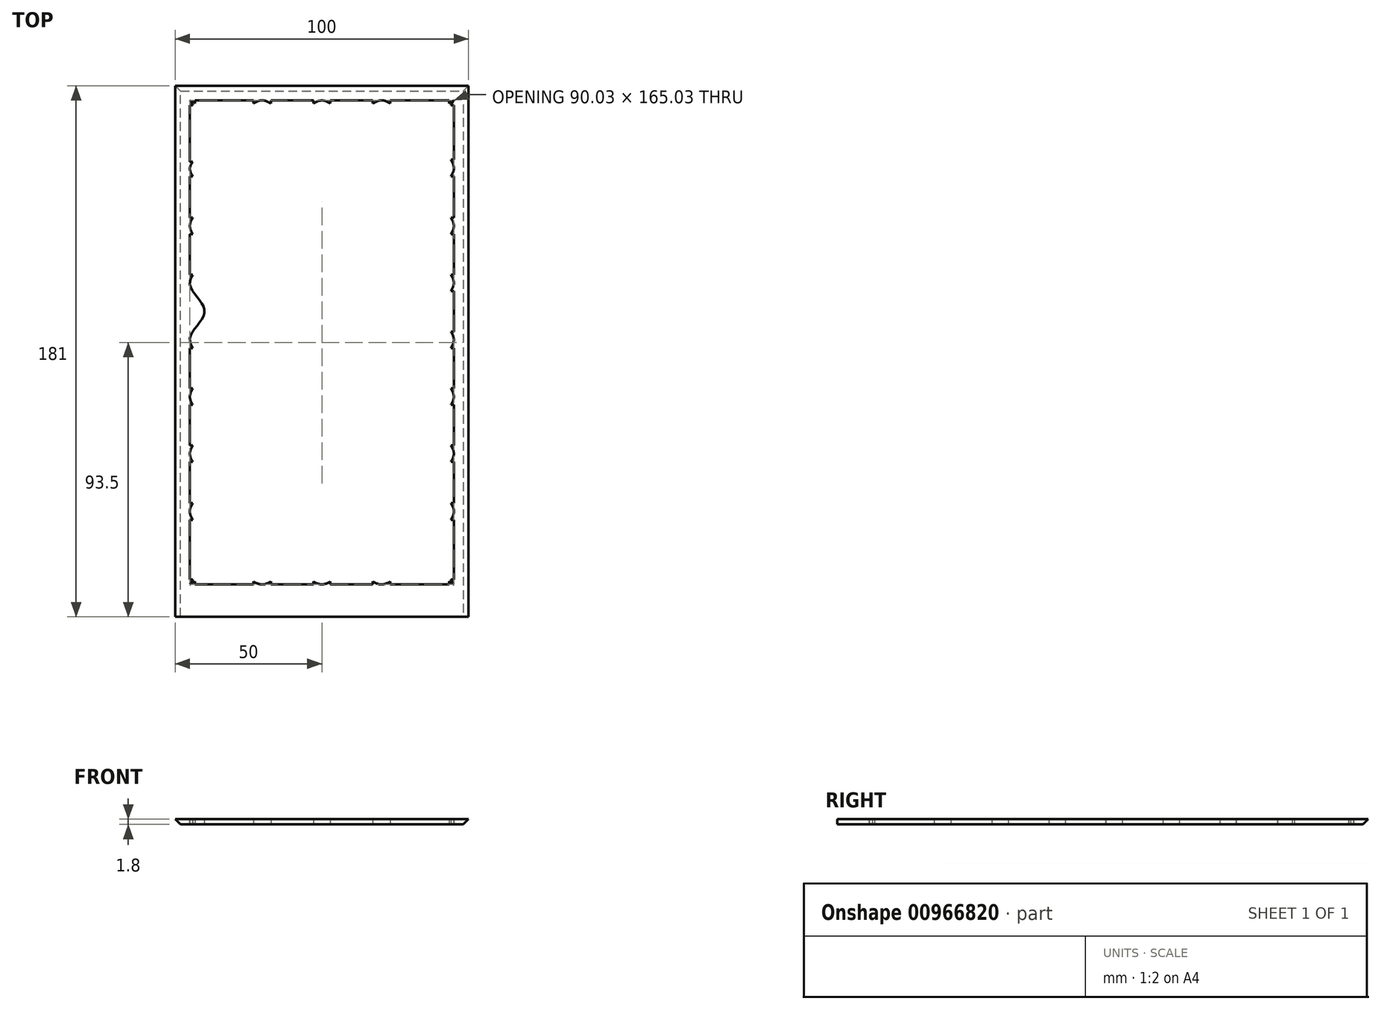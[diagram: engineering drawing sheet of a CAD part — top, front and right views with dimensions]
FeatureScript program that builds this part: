
annotation { "Feature Type Name" : "Feature", "Feature Type Description" : "" }
export const myFeature = defineFeature(function(context is Context, id is Id, definition is map)
    precondition{}
    {
        {
            var Q0;
            Q0=qCreatedBy(makeId("Top.planeOp"),FACE);
            var sketch = newSketch(context, id + "F0", { "sketchPlane" : qUnion([Q0])});
            skLineSegment(sketch, "E0.bottom", {"start": v(-50, 90) * mm, "end": v(50, 90) * mm});
            skLineSegment(sketch, "E0.left", {"start": v(-50, 90) * mm, "end": v(-50, -90) * mm});
            skLineSegment(sketch, "E0.right", {"start": v(50, 90) * mm, "end": v(50, -90) * mm});
            skLineSegment(sketch, "E1.bottom", {"start": v(-43.3, 85) * mm, "end": v(-23.33, 85) * mm});
            skLineSegment(sketch, "E1.top", {"start": v(-43.3, -80) * mm, "end": v(-23.33, -80) * mm});
            skLineSegment(sketch, "E1.left", {"start": v(-45, 83.32) * mm, "end": v(-45, 64.07) * mm});
            skLineSegment(sketch, "E1.right", {"start": v(45, 83.36) * mm, "end": v(45, 64.83) * mm});
            skFitSpline(sketch, "E2", {"points": [v(-45, 85) * mm, v(-30, 80) * mm, v(-20, 85) * mm, v(-10, 80) * mm, v(0, 85) * mm, v(10, 80) * mm, v(20, 85) * mm, v(30, 80) * mm, v(45, 85) * mm], "startDerivative": vector(112.01, -66.4) * mm, "endDerivative": vector(112.01, 66.4) * mm});
            skLineSegment(sketch, "E3", {"start": v(-45, 6.18) * mm, "end": v(-45, 20.01) * mm, "construction": true});
            skFitSpline(sketch, "E4", {"points": [v(-45, 85) * mm, v(-40, 69.3) * mm, v(-45, 61.6) * mm, v(-40, 51.9) * mm, v(-45, 42.2) * mm, v(-40, 32.5) * mm, v(-45, 22.8) * mm, v(-40, 13.1) * mm, v(-45, 3.4) * mm, v(-40, -6.3) * mm, v(-45, -16) * mm, v(-40, -25.7) * mm, v(-45, -35.4) * mm, v(-40, -45.1) * mm, v(-45, -54.8) * mm, v(-40, -64.4) * mm, v(-45, -80) * mm], "startDerivative": vector(129.63, -214.28) * mm, "endDerivative": vector(-130, -213.67) * mm});
            skFitSpline(sketch, "E5.trimOffspring", {"points": [v(-45, 85) * mm, v(-40, 69.3) * mm, v(-45, 61.6) * mm, v(-40, 51.9) * mm, v(-45, 42.2) * mm, v(-40, 32.5) * mm, v(-45, 22.8) * mm, v(-40, 13.1) * mm, v(-45, 3.4) * mm, v(-40, -6.3) * mm, v(-45, -16) * mm, v(-40, -25.7) * mm, v(-45, -35.4) * mm, v(-40, -45.1) * mm, v(-45, -54.8) * mm, v(-40, -64.4) * mm, v(-45, -80) * mm], "startDerivative": vector(129.63, -214.28) * mm, "endDerivative": vector(-130, -213.67) * mm});
            skFitSpline(sketch, "E6.trimOffspring", {"points": [v(-45, -80) * mm, v(-30, -75) * mm, v(-20, -80) * mm, v(-10, -75) * mm, v(0, -80) * mm, v(10, -75) * mm, v(20, -80) * mm, v(30, -75) * mm, v(45, -80) * mm], "startDerivative": vector(112.01, 66.4) * mm, "endDerivative": vector(112.01, -66.4) * mm});
            skFitSpline(sketch, "E7.trimOffspring", {"points": [v(45, 85) * mm, v(40, 71.3) * mm, v(45, 61.6) * mm, v(40, 51.9) * mm, v(45, 42.2) * mm, v(40, 32.5) * mm, v(45, 22.8) * mm, v(40, 13.1) * mm, v(45, 3.4) * mm, v(40, -6.3) * mm, v(45, -16) * mm, v(40, -25.7) * mm, v(45, -35.4) * mm, v(40, -45.1) * mm, v(45, -54.8) * mm, v(40, -64.4) * mm, v(45, -80) * mm], "startDerivative": vector(-129.63, -214.28) * mm, "endDerivative": vector(130, -213.67) * mm});
            skLineSegment(sketch, "E8.trimOffspring", {"start": v(45, -16) * mm, "end": v(45, -16) * mm});
            skLineSegment(sketch, "E9.trimOffspring", {"start": v(45, 3.4) * mm, "end": v(45, 3.4) * mm});
            skLineSegment(sketch, "E10.trimOffspring", {"start": v(45, 22.8) * mm, "end": v(45, 22.8) * mm});
            skLineSegment(sketch, "E11", {"start": v(-44, 83.32) * mm, "end": v(-45, 83.32) * mm});
            skLineSegment(sketch, "E12", {"start": v(-43.3, 84) * mm, "end": v(-43.3, 85) * mm});
            skLineSegment(sketch, "E13", {"start": v(-23.33, 84) * mm, "end": v(-23.33, 85) * mm});
            skLineSegment(sketch, "E14", {"start": v(-17.4, 84) * mm, "end": v(-17.4, 85) * mm});
            skLineSegment(sketch, "E15", {"start": v(-2.88, 84) * mm, "end": v(-2.88, 85) * mm});
            skLineSegment(sketch, "E16", {"start": v(2.88, 84) * mm, "end": v(2.88, 85) * mm});
            skLineSegment(sketch, "E17", {"start": v(17.4, 84) * mm, "end": v(17.4, 85) * mm});
            skLineSegment(sketch, "E18", {"start": v(23.33, 84) * mm, "end": v(23.33, 85) * mm});
            skLineSegment(sketch, "E19", {"start": v(43.3, 84) * mm, "end": v(43.3, 85) * mm});
            skLineSegment(sketch, "E20", {"start": v(44, 83.36) * mm, "end": v(45, 83.36) * mm});
            skLineSegment(sketch, "E21", {"start": v(44, 64.83) * mm, "end": v(45, 64.83) * mm});
            skLineSegment(sketch, "E22", {"start": v(44, 59.05) * mm, "end": v(45, 59.05) * mm});
            skLineSegment(sketch, "E23", {"start": v(44, 45.01) * mm, "end": v(45, 45.01) * mm});
            skLineSegment(sketch, "E24", {"start": v(44, 39.43) * mm, "end": v(45, 39.43) * mm});
            skLineSegment(sketch, "E25", {"start": v(44, 25.58) * mm, "end": v(45, 25.58) * mm});
            skLineSegment(sketch, "E26", {"start": v(44, 20.01) * mm, "end": v(45, 20.01) * mm});
            skLineSegment(sketch, "E27", {"start": v(44, 6.18) * mm, "end": v(45, 6.18) * mm});
            skLineSegment(sketch, "E28", {"start": v(44, 0.61) * mm, "end": v(45, 0.61) * mm});
            skLineSegment(sketch, "E29", {"start": v(44, -18.8) * mm, "end": v(45, -18.8) * mm});
            skLineSegment(sketch, "E30", {"start": v(44, -13.22) * mm, "end": v(45, -13.22) * mm});
            skLineSegment(sketch, "E31", {"start": v(44, -32.64) * mm, "end": v(45, -32.64) * mm});
            skLineSegment(sketch, "E32", {"start": v(44, -38.22) * mm, "end": v(45, -38.22) * mm});
            skLineSegment(sketch, "E33", {"start": v(44, -52.3) * mm, "end": v(45, -52.3) * mm});
            skLineSegment(sketch, "E34", {"start": v(44, -58) * mm, "end": v(45, -58) * mm});
            skLineSegment(sketch, "E35", {"start": v(43.3, -79) * mm, "end": v(43.3, -80) * mm});
            skLineSegment(sketch, "E36", {"start": v(44, -78.33) * mm, "end": v(45, -78.33) * mm});
            skLineSegment(sketch, "E37", {"start": v(23.33, -79) * mm, "end": v(23.33, -80) * mm});
            skLineSegment(sketch, "E38", {"start": v(17.4, -79) * mm, "end": v(17.4, -80) * mm});
            skLineSegment(sketch, "E39", {"start": v(2.88, -79) * mm, "end": v(2.88, -80) * mm});
            skLineSegment(sketch, "E40", {"start": v(2.88, -80) * mm, "end": v(2.87, -79.93) * mm});
            skLineSegment(sketch, "E41", {"start": v(-2.88, -79) * mm, "end": v(-2.88, -80) * mm});
            skLineSegment(sketch, "E42", {"start": v(-17.4, -79) * mm, "end": v(-17.4, -80) * mm});
            skLineSegment(sketch, "E43", {"start": v(-23.33, -79) * mm, "end": v(-23.33, -80) * mm});
            skLineSegment(sketch, "E44", {"start": v(-43.3, -79) * mm, "end": v(-43.3, -80) * mm});
            skLineSegment(sketch, "E45", {"start": v(-44, -78.33) * mm, "end": v(-45, -78.33) * mm});
            skLineSegment(sketch, "E46", {"start": v(-44, -58) * mm, "end": v(-45, -58) * mm});
            skLineSegment(sketch, "E47", {"start": v(-44, -52.3) * mm, "end": v(-45, -52.3) * mm});
            skLineSegment(sketch, "E48", {"start": v(-44, -38.22) * mm, "end": v(-45, -38.22) * mm});
            skLineSegment(sketch, "E49", {"start": v(-44, -32.64) * mm, "end": v(-45, -32.64) * mm});
            skLineSegment(sketch, "E50", {"start": v(-44, -18.8) * mm, "end": v(-45, -18.8) * mm});
            skLineSegment(sketch, "E51", {"start": v(-44, -13.22) * mm, "end": v(-45, -13.22) * mm});
            skLineSegment(sketch, "E52", {"start": v(-44, 0.61) * mm, "end": v(-45, 0.61) * mm});
            skLineSegment(sketch, "E53", {"start": v(-44, 6.18) * mm, "end": v(-45, 6.18) * mm});
            skLineSegment(sketch, "E54", {"start": v(-44, 20.01) * mm, "end": v(-45, 20.01) * mm});
            skLineSegment(sketch, "E55", {"start": v(-44, 25.58) * mm, "end": v(-45, 25.58) * mm});
            skLineSegment(sketch, "E56", {"start": v(-44, 39.43) * mm, "end": v(-45, 39.43) * mm});
            skLineSegment(sketch, "E57", {"start": v(-44, 44.96) * mm, "end": v(-45, 44.96) * mm});
            skLineSegment(sketch, "E58", {"start": v(-44, 59.1) * mm, "end": v(-45, 59.1) * mm});
            skLineSegment(sketch, "E59", {"start": v(-44, 64.07) * mm, "end": v(-45, 64.07) * mm});
            skLineSegment(sketch, "E60.trimOffspring", {"start": v(-17.4, 85) * mm, "end": v(-2.88, 85) * mm});
            skLineSegment(sketch, "E61.trimOffspring", {"start": v(2.88, 85) * mm, "end": v(17.4, 85) * mm});
            skLineSegment(sketch, "E62.trimOffspring", {"start": v(23.33, 85) * mm, "end": v(43.3, 85) * mm});
            skLineSegment(sketch, "E63.trimOffspring", {"start": v(-45, 59.1) * mm, "end": v(-45, 44.96) * mm});
            skLineSegment(sketch, "E64.trimOffspring", {"start": v(-45, 39.43) * mm, "end": v(-45, 25.58) * mm});
            skLineSegment(sketch, "E65.trimOffspring", {"start": v(-45, 20.01) * mm, "end": v(-45, 6.18) * mm});
            skLineSegment(sketch, "E66.trimOffspring", {"start": v(-45, 0.61) * mm, "end": v(-45, -13.22) * mm});
            skLineSegment(sketch, "E67.trimOffspring", {"start": v(-45, -18.8) * mm, "end": v(-45, -32.64) * mm});
            skLineSegment(sketch, "E68.trimOffspring", {"start": v(-45, -38.22) * mm, "end": v(-45, -52.3) * mm});
            skLineSegment(sketch, "E69.trimOffspring", {"start": v(-45, -58) * mm, "end": v(-45, -78.33) * mm});
            skLineSegment(sketch, "E70.trimOffspring", {"start": v(-17.4, -80) * mm, "end": v(-2.88, -80) * mm});
            skLineSegment(sketch, "E71.trimOffspring", {"start": v(2.88, -80) * mm, "end": v(17.4, -80) * mm});
            skLineSegment(sketch, "E72.trimOffspring", {"start": v(23.33, -80) * mm, "end": v(43.3, -80) * mm});
            skLineSegment(sketch, "E73.trimOffspring", {"start": v(45, -58) * mm, "end": v(45, -78.33) * mm});
            skLineSegment(sketch, "E74.trimOffspring", {"start": v(45, -38.22) * mm, "end": v(45, -52.3) * mm});
            skLineSegment(sketch, "E75.trimOffspring", {"start": v(45, -18.8) * mm, "end": v(45, -32.64) * mm});
            skLineSegment(sketch, "E76.trimOffspring", {"start": v(45, 0.61) * mm, "end": v(45, -13.22) * mm});
            skLineSegment(sketch, "E77.trimOffspring", {"start": v(45, 20.01) * mm, "end": v(45, 6.18) * mm});
            skLineSegment(sketch, "E78.trimOffspring", {"start": v(45, 39.43) * mm, "end": v(45, 25.58) * mm});
            skLineSegment(sketch, "E79.trimOffspring", {"start": v(45, 59.05) * mm, "end": v(45, 45.01) * mm});
            skLineSegment(sketch, "E80.top", {"start": v(-50, -91) * mm, "end": v(50, -91) * mm});
            skLineSegment(sketch, "E80.left", {"start": v(-50, -90) * mm, "end": v(-50, -91) * mm});
            skLineSegment(sketch, "E80.right", {"start": v(50, -90) * mm, "end": v(50, -91) * mm});
            skLineSegment(sketch, "E81", {"start": v(31.2, 50.15) * mm, "end": v(20.89, 51.97) * mm});
            skLineSegment(sketch, "E82", {"start": v(20.89, 51.97) * mm, "end": v(13.55, 44.5) * mm});
            skLineSegment(sketch, "E83", {"start": v(13.55, 44.5) * mm, "end": v(12.09, 54.87) * mm});
            skLineSegment(sketch, "E84", {"start": v(12.09, 54.87) * mm, "end": v(2.71, 59.55) * mm});
            skLineSegment(sketch, "E85", {"start": v(2.71, 59.55) * mm, "end": v(12.13, 64.14) * mm});
            skLineSegment(sketch, "E86", {"start": v(12.13, 64.14) * mm, "end": v(13.68, 74.5) * mm});
            skLineSegment(sketch, "E87", {"start": v(13.68, 74.5) * mm, "end": v(20.96, 66.97) * mm});
            skLineSegment(sketch, "E88", {"start": v(20.96, 66.97) * mm, "end": v(31.29, 68.7) * mm});
            skLineSegment(sketch, "E89", {"start": v(31.29, 68.7) * mm, "end": v(26.37, 59.44) * mm});
            skLineSegment(sketch, "E90", {"start": v(26.37, 59.44) * mm, "end": v(31.2, 50.15) * mm});
            skLineSegment(sketch, "E91", {"start": v(-4.34, 36.06) * mm, "end": v(-14.46, 33.34) * mm});
            skLineSegment(sketch, "E92", {"start": v(-14.46, 33.34) * mm, "end": v(-17.96, 23.47) * mm});
            skLineSegment(sketch, "E93", {"start": v(-17.96, 23.47) * mm, "end": v(-23.67, 32.26) * mm});
            skLineSegment(sketch, "E94", {"start": v(-23.67, 32.26) * mm, "end": v(-34.14, 32.53) * mm});
            skLineSegment(sketch, "E95", {"start": v(-34.14, 32.53) * mm, "end": v(-27.55, 40.67) * mm});
            skLineSegment(sketch, "E96", {"start": v(-27.55, 40.67) * mm, "end": v(-30.52, 50.72) * mm});
            skLineSegment(sketch, "E97", {"start": v(-30.52, 50.72) * mm, "end": v(-20.74, 46.97) * mm});
            skLineSegment(sketch, "E98", {"start": v(-20.74, 46.97) * mm, "end": v(-12.1, 52.9) * mm});
            skLineSegment(sketch, "E99", {"start": v(-12.1, 52.9) * mm, "end": v(-12.65, 42.44) * mm});
            skLineSegment(sketch, "E100", {"start": v(-12.65, 42.44) * mm, "end": v(-4.34, 36.06) * mm});
            skLineSegment(sketch, "E101", {"start": v(35.05, -32.75) * mm, "end": v(24.74, -34.57) * mm});
            skLineSegment(sketch, "E102", {"start": v(24.74, -34.57) * mm, "end": v(20.4, -44.1) * mm});
            skLineSegment(sketch, "E103", {"start": v(20.4, -44.1) * mm, "end": v(15.47, -34.85) * mm});
            skLineSegment(sketch, "E104", {"start": v(15.47, -34.85) * mm, "end": v(5.07, -33.66) * mm});
            skLineSegment(sketch, "E105", {"start": v(5.07, -33.66) * mm, "end": v(12.34, -26.13) * mm});
            skLineSegment(sketch, "E106", {"start": v(12.34, -26.13) * mm, "end": v(10.26, -15.86) * mm});
            skLineSegment(sketch, "E107", {"start": v(10.26, -15.86) * mm, "end": v(19.67, -20.45) * mm});
            skLineSegment(sketch, "E108", {"start": v(19.67, -20.45) * mm, "end": v(28.79, -15.3) * mm});
            skLineSegment(sketch, "E109", {"start": v(28.79, -15.3) * mm, "end": v(27.33, -25.67) * mm});
            skLineSegment(sketch, "E110", {"start": v(27.33, -25.67) * mm, "end": v(35.05, -32.75) * mm});
            skLineSegment(sketch, "E111", {"start": v(-3.19, -47.65) * mm, "end": v(-12.25, -52.9) * mm});
            skLineSegment(sketch, "E112", {"start": v(-12.25, -52.9) * mm, "end": v(-13.08, -63.34) * mm});
            skLineSegment(sketch, "E113", {"start": v(-13.08, -63.34) * mm, "end": v(-20.87, -56.33) * mm});
            skLineSegment(sketch, "E114", {"start": v(-20.87, -56.33) * mm, "end": v(-31.05, -58.77) * mm});
            skLineSegment(sketch, "E115", {"start": v(-31.05, -58.77) * mm, "end": v(-26.8, -49.2) * mm});
            skLineSegment(sketch, "E116", {"start": v(-26.8, -49.2) * mm, "end": v(-32.26, -40.27) * mm});
            skLineSegment(sketch, "E117", {"start": v(-32.26, -40.27) * mm, "end": v(-21.85, -41.36) * mm});
            skLineSegment(sketch, "E118", {"start": v(-21.85, -41.36) * mm, "end": v(-15.04, -33.4) * mm});
            skLineSegment(sketch, "E119", {"start": v(-15.04, -33.4) * mm, "end": v(-12.86, -43.64) * mm});
            skLineSegment(sketch, "E120", {"start": v(-12.86, -43.64) * mm, "end": v(-3.19, -47.65) * mm});
            skLineSegment(sketch, "E121", {"start": v(23.76, 6.66) * mm, "end": v(10.83, 1.37) * mm});
            skLineSegment(sketch, "E122", {"start": v(10.83, 1.37) * mm, "end": v(7.86, -12.27) * mm});
            skLineSegment(sketch, "E123", {"start": v(7.86, -12.27) * mm, "end": v(-1.16, -1.61) * mm});
            skLineSegment(sketch, "E124", {"start": v(-1.16, -1.61) * mm, "end": v(-15.06, -3) * mm});
            skLineSegment(sketch, "E125", {"start": v(-15.06, -3) * mm, "end": v(-7.7, 8.87) * mm});
            skLineSegment(sketch, "E126", {"start": v(-7.7, 8.87) * mm, "end": v(-13.32, 21.66) * mm});
            skLineSegment(sketch, "E127", {"start": v(-13.32, 21.66) * mm, "end": v(0.24, 18.34) * mm});
            skLineSegment(sketch, "E128", {"start": v(0.24, 18.34) * mm, "end": v(10.67, 27.63) * mm});
            skLineSegment(sketch, "E129", {"start": v(10.67, 27.63) * mm, "end": v(11.7, 13.7) * mm});
            skLineSegment(sketch, "E130", {"start": v(11.7, 13.7) * mm, "end": v(23.76, 6.66) * mm});
            skLineSegment(sketch, "E131", {"start": v(31.45, -63.35) * mm, "end": v(26.3, -62.44) * mm});
            skLineSegment(sketch, "E132", {"start": v(26.3, -62.44) * mm, "end": v(22.62, -66.17) * mm});
            skLineSegment(sketch, "E133", {"start": v(22.62, -66.17) * mm, "end": v(21.9, -60.99) * mm});
            skLineSegment(sketch, "E134", {"start": v(21.9, -60.99) * mm, "end": v(17.2, -58.65) * mm});
            skLineSegment(sketch, "E135", {"start": v(17.2, -58.65) * mm, "end": v(21.91, -56.35) * mm});
            skLineSegment(sketch, "E136", {"start": v(21.91, -56.35) * mm, "end": v(22.7, -51.17) * mm});
            skLineSegment(sketch, "E137", {"start": v(22.7, -51.17) * mm, "end": v(26.33, -54.94) * mm});
            skLineSegment(sketch, "E138", {"start": v(26.33, -54.94) * mm, "end": v(31.5, -54.08) * mm});
            skLineSegment(sketch, "E139", {"start": v(31.5, -54.08) * mm, "end": v(29.04, -58.7) * mm});
            skLineSegment(sketch, "E140", {"start": v(29.04, -58.7) * mm, "end": v(31.45, -63.35) * mm});
            skLineSegment(sketch, "E141", {"start": v(-24.78, -26.64) * mm, "end": v(-27.63, -22.24) * mm});
            skLineSegment(sketch, "E142", {"start": v(-27.63, -22.24) * mm, "end": v(-32.86, -22.09) * mm});
            skLineSegment(sketch, "E143", {"start": v(-32.86, -22.09) * mm, "end": v(-29.55, -18.03) * mm});
            skLineSegment(sketch, "E144", {"start": v(-29.55, -18.03) * mm, "end": v(-31.02, -13) * mm});
            skLineSegment(sketch, "E145", {"start": v(-31.02, -13) * mm, "end": v(-26.14, -14.9) * mm});
            skLineSegment(sketch, "E146", {"start": v(-26.14, -14.9) * mm, "end": v(-21.82, -11.94) * mm});
            skLineSegment(sketch, "E147", {"start": v(-21.82, -11.94) * mm, "end": v(-22.1, -17.17) * mm});
            skLineSegment(sketch, "E148", {"start": v(-22.1, -17.17) * mm, "end": v(-17.96, -20.37) * mm});
            skLineSegment(sketch, "E149", {"start": v(-17.96, -20.37) * mm, "end": v(-23.02, -21.71) * mm});
            skLineSegment(sketch, "E150", {"start": v(-23.02, -21.71) * mm, "end": v(-24.78, -26.64) * mm});
            skLineSegment(sketch, "E151", {"start": v(-9.58, 59.24) * mm, "end": v(-13.6, 62.6) * mm});
            skLineSegment(sketch, "E152", {"start": v(-13.6, 62.6) * mm, "end": v(-18.64, 61.2) * mm});
            skLineSegment(sketch, "E153", {"start": v(-18.64, 61.2) * mm, "end": v(-16.68, 66.06) * mm});
            skLineSegment(sketch, "E154", {"start": v(-16.68, 66.06) * mm, "end": v(-19.57, 70.43) * mm});
            skLineSegment(sketch, "E155", {"start": v(-19.57, 70.43) * mm, "end": v(-14.34, 70.07) * mm});
            skLineSegment(sketch, "E156", {"start": v(-14.34, 70.07) * mm, "end": v(-11.08, 74.16) * mm});
            skLineSegment(sketch, "E157", {"start": v(-11.08, 74.16) * mm, "end": v(-9.81, 69.08) * mm});
            skLineSegment(sketch, "E158", {"start": v(-9.81, 69.08) * mm, "end": v(-4.9, 67.25) * mm});
            skLineSegment(sketch, "E159", {"start": v(-4.9, 67.25) * mm, "end": v(-9.35, 64.47) * mm});
            skLineSegment(sketch, "E160", {"start": v(-9.35, 64.47) * mm, "end": v(-9.58, 59.24) * mm});
            skPoint(sketch, "E161", {"position": v(-16.42, 49.93) * mm});
            skSolve(sketch);
        }
        {
            var Q0;
            Q0 = qSketchRegion(id + "F0", true);
            extrude(context, id + "F1", {"entities" : qUnion([Q0]), "depth" : 1.8 * mm, "offsetDistance" : 25 * mm});
        }
        {
            var Q0;
            Q0=makeQuery(id+"F1.opExtrude","CAP_EDGE",EDGE,{"disambiguationData":[OSD([sQuery(id+"F0.wireOp",EDGE,"E0.bottom")])],"isStart":true});
            var Q1;
            Q1=makeQuery(id+"F1.opExtrude","CAP_EDGE",EDGE,{"disambiguationData":[OSD([sQuery(id+"F0.wireOp",EDGE,"E0.left")])],"isStart":true});
            var Q2;
            Q2=makeQuery(id+"F1.opExtrude","CAP_EDGE",EDGE,{"disambiguationData":[OSD([sQuery(id+"F0.wireOp",EDGE,"E0.right")])],"isStart":true});
            chamfer(context, id + "F2", {"entities" : qUnion([Q0, Q1, Q2]), "width" : 1.8 * mm, "tangentPropagation" : true});
        }
    });
